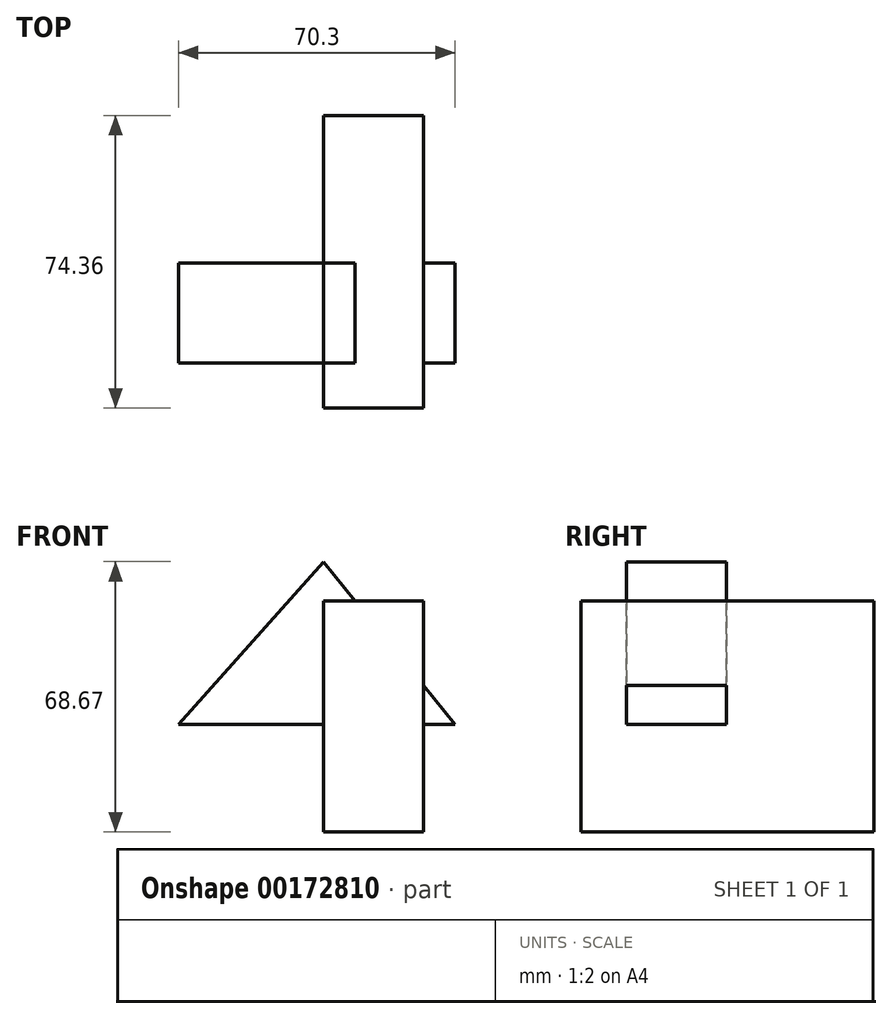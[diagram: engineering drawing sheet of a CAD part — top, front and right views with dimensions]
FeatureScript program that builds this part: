
annotation { "Feature Type Name" : "Feature", "Feature Type Description" : "" }
export const myFeature = defineFeature(function(context is Context, id is Id, definition is map)
    precondition{}
    {
        {
            var Q0;
            Q0=qCreatedBy(makeId("Front.planeOp"),FACE);
            var sketch = newSketch(context, id + "F0", { "sketchPlane" : qUnion([Q0])});
            skLineSegment(sketch, "E0", {"start": v(0, 0) * mm, "end": v(0, 41.33) * mm});
            skLineSegment(sketch, "E1", {"start": v(0, 41.33) * mm, "end": v(-36.87, 0) * mm});
            skLineSegment(sketch, "E2", {"start": v(-36.87, 0) * mm, "end": v(33.43, 0) * mm});
            skLineSegment(sketch, "E3", {"start": v(33.43, 0) * mm, "end": v(0, 41.33) * mm});
            skSolve(sketch);
        }
        {
            var Q0;
            Q0=qCreatedBy(makeId("Right.planeOp"),FACE);
            var sketch = newSketch(context, id + "F1", { "sketchPlane" : qUnion([Q0])});
            skLineSegment(sketch, "E4.bottom", {"start": v(-36.87, 31.4) * mm, "end": v(37.5, 31.4) * mm});
            skLineSegment(sketch, "E4.top", {"start": v(-36.87, -27.34) * mm, "end": v(37.5, -27.34) * mm});
            skLineSegment(sketch, "E4.left", {"start": v(-36.87, 31.4) * mm, "end": v(-36.87, -27.34) * mm});
            skLineSegment(sketch, "E4.right", {"start": v(37.5, 31.4) * mm, "end": v(37.5, -27.34) * mm});
            skSolve(sketch);
        }
        {
            var Q0;
            Q0 = qSketchRegion(id + "F0", true);
            extrude(context, id + "F2", {"entities" : qUnion([Q0]), "depth" : 25.4 * mm});
        }
        {
            var Q0;
            Q0 = qSketchRegion(id + "F1", true);
            extrude(context, id + "F3", {"entities" : qUnion([Q0]), "operationType" : NewBodyOperationType.ADD, "depth" : 25.4 * mm});
        }
    });
